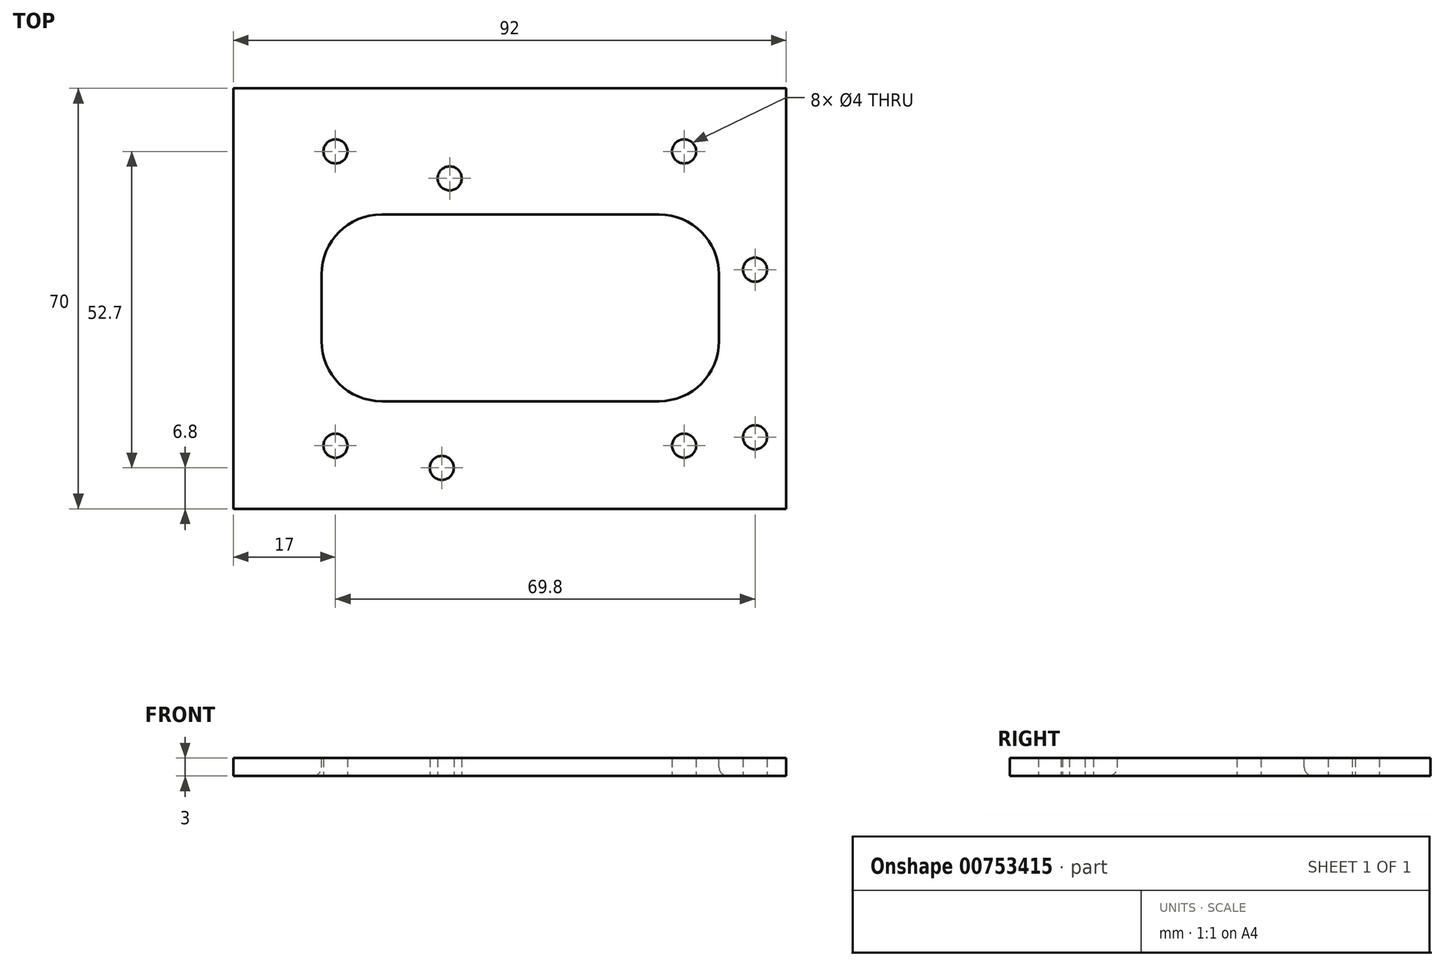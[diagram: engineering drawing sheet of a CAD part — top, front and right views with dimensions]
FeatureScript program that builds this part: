
annotation { "Feature Type Name" : "Feature", "Feature Type Description" : "" }
export const myFeature = defineFeature(function(context is Context, id is Id, definition is map)
    precondition{}
    {
        {
            var Q0;
            Q0=qCreatedBy(makeId("Top.planeOp"),FACE);
            var sketch = newSketch(context, id + "F0", { "sketchPlane" : qUnion([Q0])});
            skLineSegment(sketch, "E0.bottom", {"start": v(46, 35) * mm, "end": v(-46, 35) * mm});
            skLineSegment(sketch, "E0.top", {"start": v(46, -35) * mm, "end": v(-46, -35) * mm});
            skLineSegment(sketch, "E0.left", {"start": v(46, 35) * mm, "end": v(46, -35) * mm});
            skLineSegment(sketch, "E0.right", {"start": v(-46, 35) * mm, "end": v(-46, -35) * mm});
            skPoint(sketch, "E0.middle", {"position": v(0, 0) * mm});
            skLineSegment(sketch, "E1.bottom", {"start": v(29, 24.5) * mm, "end": v(-29, 24.5) * mm, "construction": true});
            skLineSegment(sketch, "E1.top", {"start": v(29, -24.5) * mm, "end": v(-29, -24.5) * mm, "construction": true});
            skLineSegment(sketch, "E1.left", {"start": v(29, 24.5) * mm, "end": v(29, -24.5) * mm, "construction": true});
            skLineSegment(sketch, "E1.right", {"start": v(-29, 24.5) * mm, "end": v(-29, -24.5) * mm, "construction": true});
            skLineSegment(sketch, "E2", {"start": v(-10, 20) * mm, "end": v(-10, -28.2) * mm});
            skLineSegment(sketch, "E3", {"start": v(-10, -28.2) * mm, "end": v(40.8, -28.2) * mm});
            skLineSegment(sketch, "E4", {"start": v(40.8, -28.2) * mm, "end": v(40.8, -23.1) * mm});
            skLineSegment(sketch, "E5", {"start": v(40.8, -23.1) * mm, "end": v(40.8, 4.8) * mm});
            skLineSegment(sketch, "E6", {"start": v(-10, -28.2) * mm, "end": v(-11.3, -28.2) * mm});
            skCircle(sketch, "E7", {"center": v(-11.3, -28.2) * mm, "radius": 2 * mm});
            skCircle(sketch, "E8", {"center": v(-10, 20) * mm, "radius": 2 * mm});
            skCircle(sketch, "E9", {"center": v(-29, 24.5) * mm, "radius": 2 * mm});
            skCircle(sketch, "E10", {"center": v(29, 24.5) * mm, "radius": 2 * mm});
            skCircle(sketch, "E11", {"center": v(40.8, 4.8) * mm, "radius": 2 * mm});
            skCircle(sketch, "E12", {"center": v(40.8, -23.1) * mm, "radius": 2 * mm});
            skCircle(sketch, "E13", {"center": v(29, -24.5) * mm, "radius": 2 * mm});
            skCircle(sketch, "E14", {"center": v(-29, -24.5) * mm, "radius": 2 * mm});
            skSolve(sketch);
        }
        {
            var Q0;
            Q0=makeQuery(id+"F0.imprint","IMPRINT",FACE,{"disambiguationData":[TD([[makeQuery(id+"F0.imprint","IMPRINT",EDGE,{"derivedFrom":sQuery(id+"F0.wireOp",EDGE,"E0.bottom")}),1.0]])]});
            extrude(context, id + "F1", {"entities" : qUnion([Q0]), "depth" : 3 * mm, "offsetDistance" : 25 * mm});
        }
        {
            var Q0;
            Q0=makeQuery(id+"F1.opExtrude","CAP_FACE",FACE,{"disambiguationData":[OSD([sQuery(id+"F0.wireOp",EDGE,"E0.bottom"),sQuery(id+"F0.wireOp",EDGE,"E0.top"),sQuery(id+"F0.wireOp",EDGE,"E0.left"),sQuery(id+"F0.wireOp",EDGE,"E0.right"),sQuery(id+"F0.wireOp",EDGE,"E7"),sQuery(id+"F0.wireOp",EDGE,"E8"),sQuery(id+"F0.wireOp",EDGE,"E9"),sQuery(id+"F0.wireOp",EDGE,"E10"),sQuery(id+"F0.wireOp",EDGE,"E11"),sQuery(id+"F0.wireOp",EDGE,"E12"),sQuery(id+"F0.wireOp",EDGE,"E13"),sQuery(id+"F0.wireOp",EDGE,"E14")])],"isStart":false});
            var sketch = newSketch(context, id + "F2", { "sketchPlane" : qUnion([Q0])});
            skLineSegment(sketch, "E15.0.0", {"start": v(-46, -35) * mm, "end": v(46, -35) * mm});
            skLineSegment(sketch, "E15.0.1", {"start": v(46, -35) * mm, "end": v(46, 35) * mm});
            skLineSegment(sketch, "E15.0.2", {"start": v(46, 35) * mm, "end": v(-46, 35) * mm});
            skLineSegment(sketch, "E15.0.3", {"start": v(-46, 35) * mm, "end": v(-46, -35) * mm});
            skLineSegment(sketch, "E16.bottom", {"start": v(-46, 35) * mm, "end": v(-35, 35) * mm});
            skLineSegment(sketch, "E16.top", {"start": v(-46, -35) * mm, "end": v(-35, -35) * mm});
            skLineSegment(sketch, "E16.right", {"start": v(-35, 35) * mm, "end": v(-35, -35) * mm});
            skLineSegment(sketch, "E17.bottom", {"start": v(-46, 35) * mm, "end": v(46, 35) * mm});
            skLineSegment(sketch, "E17.top", {"start": v(-46, 30.5) * mm, "end": v(46, 30.5) * mm});
            skLineSegment(sketch, "E17.left", {"start": v(-46, 35) * mm, "end": v(-46, 30.5) * mm});
            skLineSegment(sketch, "E17.right", {"start": v(46, 35) * mm, "end": v(46, 30.5) * mm});
            skLineSegment(sketch, "E18.bottom", {"start": v(-31.3, 14) * mm, "end": v(34.8, 14) * mm});
            skLineSegment(sketch, "E18.top", {"start": v(-31.3, -17.1) * mm, "end": v(34.8, -17.1) * mm});
            skLineSegment(sketch, "E18.left", {"start": v(-31.3, 14) * mm, "end": v(-31.3, -17.1) * mm});
            skLineSegment(sketch, "E18.right", {"start": v(34.8, 14) * mm, "end": v(34.8, -17.1) * mm});
            skLineSegment(sketch, "E19.bottom", {"start": v(46, -35) * mm, "end": v(-35, -35) * mm});
            skLineSegment(sketch, "E19.top", {"start": v(46, -34.2) * mm, "end": v(-35, -34.2) * mm});
            skLineSegment(sketch, "E19.left", {"start": v(46, -35) * mm, "end": v(46, -34.2) * mm});
            skLineSegment(sketch, "E19.right", {"start": v(-35, -35) * mm, "end": v(-35, -34.2) * mm});
            skSolve(sketch);
        }
        {
            var Q0;
            Q0=makeQuery(id+"F2.imprint","IMPRINT",FACE,{"disambiguationData":[TD([[makeQuery(id+"F2.imprint","IMPRINT",EDGE,{"derivedFrom":sQuery(id+"F2.wireOp",EDGE,"E16.top")}),-1.0]])]});
            var Q1;
            {var subQ5=sQuery(id+"F2.wireOp",EDGE,"E17.left");Q1=makeQuery(id+"F2.imprint","IMPRINT",FACE,{"disambiguationData":[TD([[makeQuery(id+"F2.imprint","IMPRINT",EDGE,{"derivedFrom":subQ5}),1.0]])]});}
            var Q2;
            {var subQ5=sQuery(id+"F2.wireOp",EDGE,"E17.right");Q2=makeQuery(id+"F2.imprint","IMPRINT",FACE,{"disambiguationData":[TD([[makeQuery(id+"F2.imprint","IMPRINT",EDGE,{"derivedFrom":subQ5}),-1.0]])]});}
            var Q3;
            Q3=makeQuery(id+"F2.imprint","IMPRINT",FACE,{"disambiguationData":[TD([[makeQuery(id+"F2.imprint","IMPRINT",EDGE,{"derivedFrom":sQuery(id+"F2.wireOp",EDGE,"E18.bottom")}),-1.0]])]});
            var Q4;
            Q4=makeQuery(id+"F2.imprint","IMPRINT",FACE,{"disambiguationData":[TD([[makeQuery(id+"F2.imprint","IMPRINT",EDGE,{"derivedFrom":sQuery(id+"F2.wireOp",EDGE,"E19.bottom")}),-1.0]])]});
            extrude(context, id + "F3", {"entities" : qUnion([Q0, Q1, Q2, Q3, Q4]), "operationType" : NewBodyOperationType.REMOVE, "endBound" : BoundingType.THROUGH_ALL, "oppositeDirection" : true, "depth" : 25 * mm, "offsetDistance" : 25 * mm});
        }
        {
            var Q0;
            Q0=makeQuery(id+"F3.boolean.opBoolean","COPY",EDGE,{"derivedFrom":makeQuery(id+"F3.opExtrude","SWEPT_EDGE",EDGE,{"disambiguationData":[OSD([sQuery(id+"F2.wireOp",EDGE,"E16.right"),sQuery(id+"F2.wireOp",EDGE,"E17.top")])]})});
            var Q1;
            Q1=makeQuery(id+"F3.boolean.opBoolean","COPY",EDGE,{"derivedFrom":makeQuery(id+"F3.opExtrude","SWEPT_EDGE",EDGE,{"disambiguationData":[OSD([sQuery(id+"F2.wireOp",EDGE,"E16.right"),sQuery(id+"F2.wireOp",EDGE,"E19.top"),sQuery(id+"F2.wireOp",EDGE,"E19.right")])]})});
            var Q2;
            Q2=makeQuery(id+"F3.boolean.opBoolean","COPY",EDGE,{"derivedFrom":makeQuery(id+"F3.opExtrude","SWEPT_EDGE",EDGE,{"disambiguationData":[OSD([sQuery(id+"F2.wireOp",EDGE,"E15.0.1"),sQuery(id+"F2.wireOp",EDGE,"E19.top"),sQuery(id+"F2.wireOp",EDGE,"E19.left")])]})});
            var Q3;
            Q3=makeQuery(id+"F3.boolean.opBoolean","COPY",EDGE,{"derivedFrom":makeQuery(id+"F3.opExtrude","SWEPT_EDGE",EDGE,{"disambiguationData":[OSD([sQuery(id+"F2.wireOp",EDGE,"E15.0.1"),sQuery(id+"F2.wireOp",EDGE,"E17.top"),sQuery(id+"F2.wireOp",EDGE,"E17.right")])]})});
            var Q4;
            Q4=makeQuery(id+"F3.boolean.opBoolean","COPY",EDGE,{"derivedFrom":makeQuery(id+"F3.opExtrude","SWEPT_EDGE",EDGE,{"disambiguationData":[OSD([sQuery(id+"F2.wireOp",EDGE,"E18.bottom"),sQuery(id+"F2.wireOp",EDGE,"E18.left")])]})});
            var Q5;
            Q5=makeQuery(id+"F3.boolean.opBoolean","COPY",EDGE,{"derivedFrom":makeQuery(id+"F3.opExtrude","SWEPT_EDGE",EDGE,{"disambiguationData":[OSD([sQuery(id+"F2.wireOp",EDGE,"E18.bottom"),sQuery(id+"F2.wireOp",EDGE,"E18.right")])]})});
            var Q6;
            Q6=makeQuery(id+"F3.boolean.opBoolean","COPY",EDGE,{"derivedFrom":makeQuery(id+"F3.opExtrude","SWEPT_EDGE",EDGE,{"disambiguationData":[OSD([sQuery(id+"F2.wireOp",EDGE,"E18.top"),sQuery(id+"F2.wireOp",EDGE,"E18.right")])]})});
            var Q7;
            Q7=makeQuery(id+"F3.boolean.opBoolean","COPY",EDGE,{"derivedFrom":makeQuery(id+"F3.opExtrude","SWEPT_EDGE",EDGE,{"disambiguationData":[OSD([sQuery(id+"F2.wireOp",EDGE,"E18.top"),sQuery(id+"F2.wireOp",EDGE,"E18.left")])]})});
            fillet(context, id + "F4", {"entities" : qUnion([Q0, Q1, Q2, Q3, Q4, Q5, Q6, Q7]), "radius" : 10 * mm, "tangentPropagation" : true, "allowEdgeOverflow" : false});
        }
        {
            var Q0;
            Q0=makeQuery(id+"F3.boolean.opBoolean","INTERSECT",EDGE,{"derivedFrom":[makeQuery(id+"F1.opExtrude","CAP_FACE",FACE,{"disambiguationData":[OSD([sQuery(id+"F0.wireOp",EDGE,"E0.bottom"),sQuery(id+"F0.wireOp",EDGE,"E0.top"),sQuery(id+"F0.wireOp",EDGE,"E0.left"),sQuery(id+"F0.wireOp",EDGE,"E0.right"),sQuery(id+"F0.wireOp",EDGE,"E7"),sQuery(id+"F0.wireOp",EDGE,"E8"),sQuery(id+"F0.wireOp",EDGE,"E9"),sQuery(id+"F0.wireOp",EDGE,"E10"),sQuery(id+"F0.wireOp",EDGE,"E11"),sQuery(id+"F0.wireOp",EDGE,"E12"),sQuery(id+"F0.wireOp",EDGE,"E13"),sQuery(id+"F0.wireOp",EDGE,"E14")])],"isStart":true}),makeQuery(id+"F3.opExtrude","SWEPT_FACE",FACE,{"disambiguationData":[OSD([sQuery(id+"F2.wireOp",EDGE,"E18.bottom")])]})]});
            var Q1;
            Q1=makeQuery(id+"F3.boolean.opBoolean","COPY",EDGE,{"derivedFrom":makeQuery(id+"F3.opExtrude","CAP_EDGE",EDGE,{"disambiguationData":[OSD([sQuery(id+"F2.wireOp",EDGE,"E18.bottom")])],"isStart":true})});
            var Q2;
            Q2=makeQuery(id+"F3.boolean.opBoolean","COPY",EDGE,{"derivedFrom":makeQuery(id+"F3.opExtrude","CAP_EDGE",EDGE,{"disambiguationData":[OSD([sQuery(id+"F2.wireOp",EDGE,"E19.top")])],"isStart":true})});
            var Q3;
            Q3=makeQuery(id+"F3.boolean.opBoolean","INTERSECT",EDGE,{"derivedFrom":[makeQuery(id+"F1.opExtrude","CAP_FACE",FACE,{"disambiguationData":[OSD([sQuery(id+"F0.wireOp",EDGE,"E0.bottom"),sQuery(id+"F0.wireOp",EDGE,"E0.top"),sQuery(id+"F0.wireOp",EDGE,"E0.left"),sQuery(id+"F0.wireOp",EDGE,"E0.right"),sQuery(id+"F0.wireOp",EDGE,"E7"),sQuery(id+"F0.wireOp",EDGE,"E8"),sQuery(id+"F0.wireOp",EDGE,"E9"),sQuery(id+"F0.wireOp",EDGE,"E10"),sQuery(id+"F0.wireOp",EDGE,"E11"),sQuery(id+"F0.wireOp",EDGE,"E12"),sQuery(id+"F0.wireOp",EDGE,"E13"),sQuery(id+"F0.wireOp",EDGE,"E14")])],"isStart":true}),makeQuery(id+"F3.opExtrude","SWEPT_FACE",FACE,{"disambiguationData":[OSD([sQuery(id+"F2.wireOp",EDGE,"E19.top")])]})]});
            fillet(context, id + "F5", {"entities" : qUnion([Q0, Q1, Q2, Q3]), "radius" : 1.5 * mm, "tangentPropagation" : true, "allowEdgeOverflow" : false});
        }
    });
